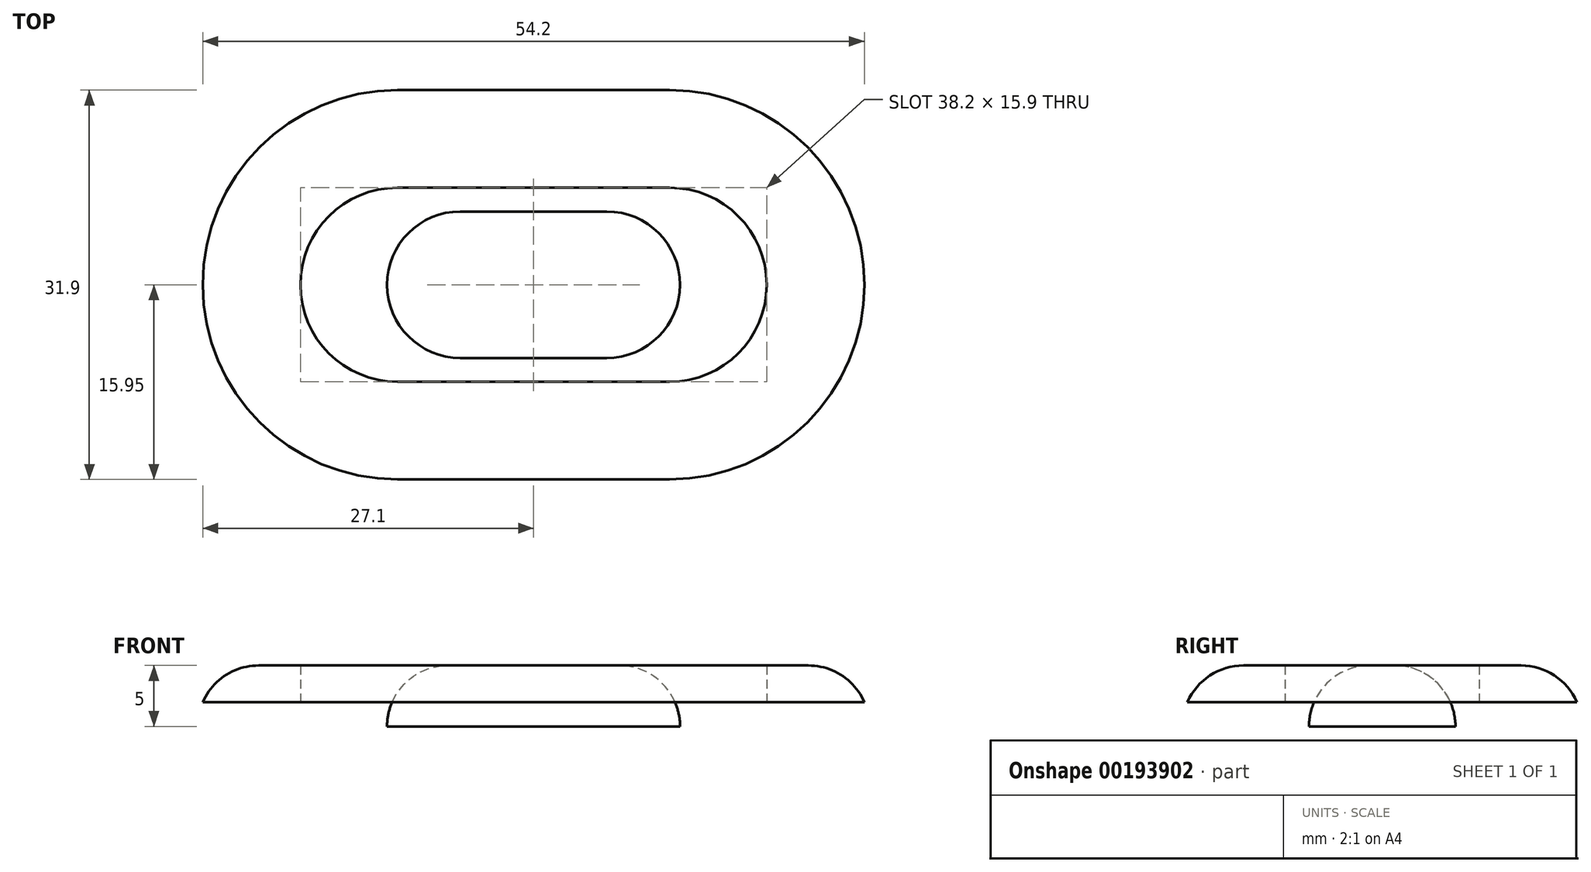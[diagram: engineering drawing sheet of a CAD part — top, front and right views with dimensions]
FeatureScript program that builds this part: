
annotation { "Feature Type Name" : "Feature", "Feature Type Description" : "" }
export const myFeature = defineFeature(function(context is Context, id is Id, definition is map)
    precondition{}
    {
        {
            var Q0;
            Q0=qCreatedBy(makeId("Top.planeOp"),FACE);
            var sketch = newSketch(context, id + "F0", { "sketchPlane" : qUnion([Q0])});
            skLineSegment(sketch, "E0", {"start": v(-12, 0) * mm, "end": v(-12, 0) * mm});
            skArc(sketch, "E1.MirrorCS", {"start": v(6, 6) * mm, "mid": v(10.24, 4.24) * mm, "end": v(12, 0) * mm});
            skLineSegment(sketch, "E2", {"start": v(6, 6) * mm, "end": v(-6, 6) * mm});
            skLineSegment(sketch, "E3", {"start": v(-6, -6) * mm, "end": v(6, -6) * mm});
            skArc(sketch, "E4", {"start": v(-6, 6) * mm, "mid": v(-12, 0) * mm, "end": v(-6, -6) * mm});
            skArc(sketch, "E5", {"start": v(6, -6) * mm, "mid": v(10.24, -4.24) * mm, "end": v(12, 0) * mm});
            skPoint(sketch, "E6.endSnap0", {"position": v(0, -6) * mm});
            skLineSegment(sketch, "E7", {"start": v(-11.15, 7.95) * mm, "end": v(-11.15, -7.95) * mm, "construction": true});
            skLineSegment(sketch, "E8", {"start": v(11.15, 7.95) * mm, "end": v(11.15, -7.95) * mm, "construction": true});
            skArc(sketch, "E9", {"start": v(11.15, -7.95) * mm, "mid": v(19.1, 0) * mm, "end": v(11.15, 7.95) * mm});
            skArc(sketch, "E10", {"start": v(-11.15, 7.95) * mm, "mid": v(-19.1, 0) * mm, "end": v(-11.15, -7.95) * mm});
            skLineSegment(sketch, "E11", {"start": v(-11.15, 7.95) * mm, "end": v(11.15, 7.95) * mm});
            skLineSegment(sketch, "E12", {"start": v(-11.15, -7.95) * mm, "end": v(11.15, -7.95) * mm});
            skLineSegment(sketch, "E13", {"start": v(-11.15, 15.95) * mm, "end": v(11.15, 15.95) * mm});
            skArc(sketch, "E14", {"start": v(11.15, 15.95) * mm, "mid": v(27.1, 0) * mm, "end": v(11.15, -15.95) * mm});
            skArc(sketch, "E15", {"start": v(-11.15, 15.95) * mm, "mid": v(-27.1, 0) * mm, "end": v(-11.15, -15.95) * mm});
            skLineSegment(sketch, "E16", {"start": v(-11.15, -15.95) * mm, "end": v(11.15, -15.95) * mm});
            skCircle(sketch, "E17", {"center": v(16.6, 0) * mm, "radius": 1.5 * mm});
            skCircle(sketch, "E18", {"center": v(-16.6, 0) * mm, "radius": 1.5 * mm});
            skSolve(sketch);
        }
        {
            var Q0;
            Q0=makeQuery(id+"F0.imprint","IMPRINT",FACE,{"disambiguationData":[TD([[makeQuery(id+"F0.imprint","IMPRINT",EDGE,{"derivedFrom":sQuery(id+"F0.wireOp",EDGE,"E1.MirrorCS")}),1.0]])]});
            extrude(context, id + "F1", {"entities" : qUnion([Q0]), "oppositeDirection" : true, "depth" : 2 * mm});
        }
        {
            var Q0;
            Q0=makeQuery(id+"F0.imprint","IMPRINT",FACE,{"disambiguationData":[TD([[makeQuery(id+"F0.imprint","IMPRINT",EDGE,{"derivedFrom":sQuery(id+"F0.wireOp",EDGE,"E1.MirrorCS")}),1.0]])]});
            var Q1;
            Q1=makeQuery(id+"F0.imprint","IMPRINT",FACE,{"disambiguationData":[TD([[makeQuery(id+"F0.imprint","IMPRINT",EDGE,{"derivedFrom":sQuery(id+"F0.wireOp",EDGE,"E9")}),-1.0]])]});
            extrude(context, id + "F2", {"entities" : qUnion([Q0, Q1]), "operationType" : NewBodyOperationType.ADD, "depth" : 3 * mm});
        }
        {
            var Q0;
            Q0=makeQuery(id+"F2.opExtrude","CAP_EDGE",EDGE,{"disambiguationData":[OSD([sQuery(id+"F0.wireOp",EDGE,"E4")])],"isStart":false});
            var Q1;
            Q1=makeQuery(id+"F2.opExtrude","CAP_EDGE",EDGE,{"disambiguationData":[OSD([sQuery(id+"F0.wireOp",EDGE,"E2")])],"isStart":false});
            var Q2;
            Q2=makeQuery(id+"F2.opExtrude","CAP_EDGE",EDGE,{"disambiguationData":[OSD([sQuery(id+"F0.wireOp",EDGE,"E1.MirrorCS"),sQuery(id+"F0.wireOp",EDGE,"E5")])],"isStart":false});
            var Q3;
            Q3=makeQuery(id+"F2.opExtrude","CAP_EDGE",EDGE,{"disambiguationData":[OSD([sQuery(id+"F0.wireOp",EDGE,"E3")])],"isStart":false});
            fillet(context, id + "F3", {"entities" : qUnion([Q0, Q1, Q2, Q3]), "radius" : 5 * mm, "tangentPropagation" : true, "allowEdgeOverflow" : false});
        }
        {
            var Q0;
            Q0=makeQuery(id+"F2.opExtrude","CAP_EDGE",EDGE,{"disambiguationData":[OSD([sQuery(id+"F0.wireOp",EDGE,"E13")])],"isStart":false});
            fillet(context, id + "F4", {"entities" : qUnion([Q0]), "radius" : 5 * mm, "tangentPropagation" : true, "allowEdgeOverflow" : false});
        }
        {
            var Q0;
            Q0=makeQuery(id+"F1.opExtrude","SWEPT_BODY",BODY,{"disambiguationData":[OSD([sQuery(id+"F0.wireOp",EDGE,"E1.MirrorCS"),sQuery(id+"F0.wireOp",EDGE,"E2"),sQuery(id+"F0.wireOp",EDGE,"E3"),sQuery(id+"F0.wireOp",EDGE,"E4"),sQuery(id+"F0.wireOp",EDGE,"E5"),sQuery(id+"F0.wireOp",EDGE,"E9"),sQuery(id+"F0.wireOp",EDGE,"E10"),sQuery(id+"F0.wireOp",EDGE,"E11"),sQuery(id+"F0.wireOp",EDGE,"E12"),sQuery(id+"F0.wireOp",EDGE,"E17"),sQuery(id+"F0.wireOp",EDGE,"E18")])]});
            transform(context, id + "F5", {"entities" : qUnion([Q0]), "transformType" : TransformType.TRANSLATION_3D, "dx" : 0 * mm, "dy" : 28 * mm, "dz" : 23 * mm, "makeCopy" : true});
        }
        {
            var Q0;
            Q0=makeQuery(id+"F5.opPattern","COPY",BODY,{"derivedFrom":makeQuery(id+"F1.opExtrude","SWEPT_BODY",BODY,{"disambiguationData":[OSD([sQuery(id+"F0.wireOp",EDGE,"E1.MirrorCS"),sQuery(id+"F0.wireOp",EDGE,"E2"),sQuery(id+"F0.wireOp",EDGE,"E3"),sQuery(id+"F0.wireOp",EDGE,"E4"),sQuery(id+"F0.wireOp",EDGE,"E5"),sQuery(id+"F0.wireOp",EDGE,"E9"),sQuery(id+"F0.wireOp",EDGE,"E10"),sQuery(id+"F0.wireOp",EDGE,"E11"),sQuery(id+"F0.wireOp",EDGE,"E12"),sQuery(id+"F0.wireOp",EDGE,"E17"),sQuery(id+"F0.wireOp",EDGE,"E18")])]}),"instanceName":"1"});
            deleteBodies(context, id + "F6", {"entities" : qUnion([Q0])});
        }
    });
